# Revit family: Dynaco_651_All_Weather_Door
name_source: partatom
category: Doors
units: mm (PartAtom-declared; Revit-internal decimal feet)

## family parameters
Always vertical = Yes
Classification Number = 23.30.10.00
Cut with Voids When Loaded = No
Host = Wall
Room Calculation Point = No
Shared = No

## types (1)
- Dynaco_651_All_Weather_Door
    Analytic Construction = <None>
    CAD Details = https://www.arcat.com
    Define Thermal Properties by = Schematic Type
    Door Height = 12' - 0"
    Door Width = 16' - 0"
    Function = Interior
    Height = 12' - 0"
    Keynote = 08 34 00
    Manufacturer = Dynaco High Performance Doors
    Model = D-651 All Weather
    Panel Material = Arcat - Dynaco - Blue - RAL5002
    Product Page URL = https://www.arcat.com
    Specification = https://www.arcat.com
    Trim Material = Galvanied Steel
    URL = https://www.dynacodoor.us
    Wall Closure = By host
    Width = 16' - 0"

## geometry (parser evidence)
native form markers: Sweep x11
no freeform markers — native parametric forms only
